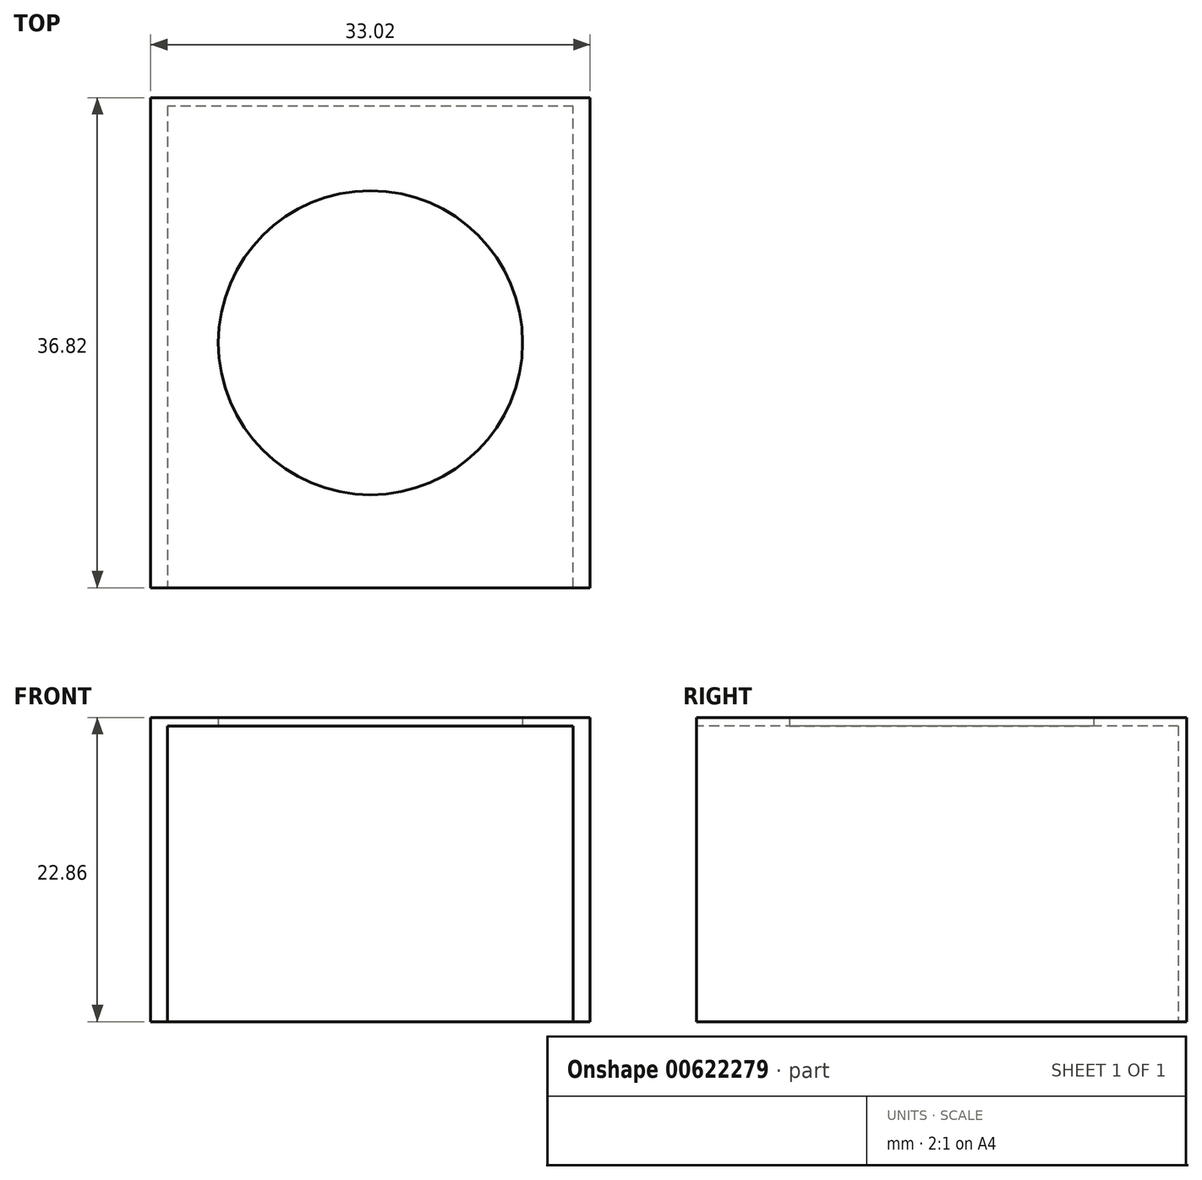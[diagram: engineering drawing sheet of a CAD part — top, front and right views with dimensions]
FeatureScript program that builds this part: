
annotation { "Feature Type Name" : "Feature", "Feature Type Description" : "" }
export const myFeature = defineFeature(function(context is Context, id is Id, definition is map)
    precondition{}
    {
        {
            var Q0;
            Q0=qCreatedBy(makeId("Top.planeOp"),FACE);
            var sketch = newSketch(context, id + "F0", { "sketchPlane" : qUnion([Q0])});
            skLineSegment(sketch, "E0", {"start": v(0, 0) * mm, "end": v(-16.51, 0) * mm});
            skLineSegment(sketch, "E1", {"start": v(-16.51, 0) * mm, "end": v(-16.51, 18.41) * mm});
            skLineSegment(sketch, "E2", {"start": v(-16.51, 18.42) * mm, "end": v(16.5, 18.42) * mm});
            skLineSegment(sketch, "E3", {"start": v(16.51, 18.41) * mm, "end": v(16.51, -18.42) * mm});
            skLineSegment(sketch, "E4", {"start": v(16.51, -18.41) * mm, "end": v(-16.51, -18.41) * mm});
            skLineSegment(sketch, "E5", {"start": v(-16.51, -18.42) * mm, "end": v(-16.51, 0) * mm});
            skSolve(sketch);
        }
        {
            var Q0;
            Q0=makeQuery(id+"F0.imprint","IMPRINT",FACE,{"disambiguationData":[TD([[makeQuery(id+"F0.imprint","IMPRINT",EDGE,{"derivedFrom":sQuery(id+"F0.wireOp",EDGE,"E1")}),-1.0]])]});
            extrude(context, id + "F1", {"entities" : qUnion([Q0]), "depth" : 22.86 * mm, "offsetDistance" : 25.4 * mm});
        }
        {
            var Q0;
            Q0=qCreatedBy(makeId("Top.planeOp"),FACE);
            var sketch = newSketch(context, id + "F2", { "sketchPlane" : qUnion([Q0])});
            skCircle(sketch, "E6", {"center": v(0, 0) * mm, "radius": 11.43 * mm});
            skSolve(sketch);
        }
        {
            var Q0;
            Q0 = qSketchRegion(id + "F2", true);
            extrude(context, id + "F3", {"entities" : qUnion([Q0]), "operationType" : NewBodyOperationType.REMOVE, "endBound" : BoundingType.THROUGH_ALL, "depth" : 25.4 * mm, "offsetDistance" : 25.4 * mm});
        }
        {
            var Q0;
            Q0=qCreatedBy(makeId("Top.planeOp"),FACE);
            var sketch = newSketch(context, id + "F4", { "sketchPlane" : qUnion([Q0])});
            skLineSegment(sketch, "E7", {"start": v(0, 0) * mm, "end": v(-15.24, 0) * mm});
            skLineSegment(sketch, "E8", {"start": v(-15.24, 0) * mm, "end": v(-15.24, -17.78) * mm});
            skLineSegment(sketch, "E9", {"start": v(15.24, -17.78) * mm, "end": v(15.24, 17.78) * mm});
            skLineSegment(sketch, "E10", {"start": v(15.24, 17.78) * mm, "end": v(-15.24, 17.78) * mm});
            skLineSegment(sketch, "E11", {"start": v(-15.24, 17.78) * mm, "end": v(-15.24, 0) * mm});
            skLineSegment(sketch, "E12", {"start": v(-15.24, -17.78) * mm, "end": v(-15.24, -25.4) * mm});
            skLineSegment(sketch, "E13", {"start": v(-15.24, -25.4) * mm, "end": v(15.24, -25.4) * mm});
            skLineSegment(sketch, "E14", {"start": v(15.24, -25.4) * mm, "end": v(15.24, -17.78) * mm});
            skSolve(sketch);
        }
        {
            var Q0;
            Q0 = qSketchRegion(id + "F4", true);
            extrude(context, id + "F5", {"entities" : qUnion([Q0]), "operationType" : NewBodyOperationType.REMOVE, "depth" : 22.22 * mm, "offsetDistance" : 25.4 * mm});
        }
        {
            var Q0;
            Q0=qCreatedBy(makeId("Top.planeOp"),FACE);
            var sketch = newSketch(context, id + "F6", { "sketchPlane" : qUnion([Q0])});
            skLineSegment(sketch, "E15", {"start": v(0, 0) * mm, "end": v(-12.57, 0) * mm});
            skLineSegment(sketch, "E16", {"start": v(-12.57, 0) * mm, "end": v(-12.57, -23.29) * mm});
            skLineSegment(sketch, "E17.MirrorCS", {"start": v(12.57, 0) * mm, "end": v(12.57, -23.29) * mm});
            skLineSegment(sketch, "E18.MirrorCS", {"start": v(0, 0) * mm, "end": v(12.57, 0) * mm});
            skLineSegment(sketch, "E19", {"start": v(-12.57, -23.29) * mm, "end": v(12.57, -23.29) * mm});
            skSolve(sketch);
        }
        {
            var Q0;
            Q0 = qSketchRegion(id + "F6", true);
            extrude(context, id + "F7", {"entities" : qUnion([Q0]), "operationType" : NewBodyOperationType.REMOVE, "depth" : 11.9 * mm, "offsetDistance" : 25.4 * mm});
        }
    });
